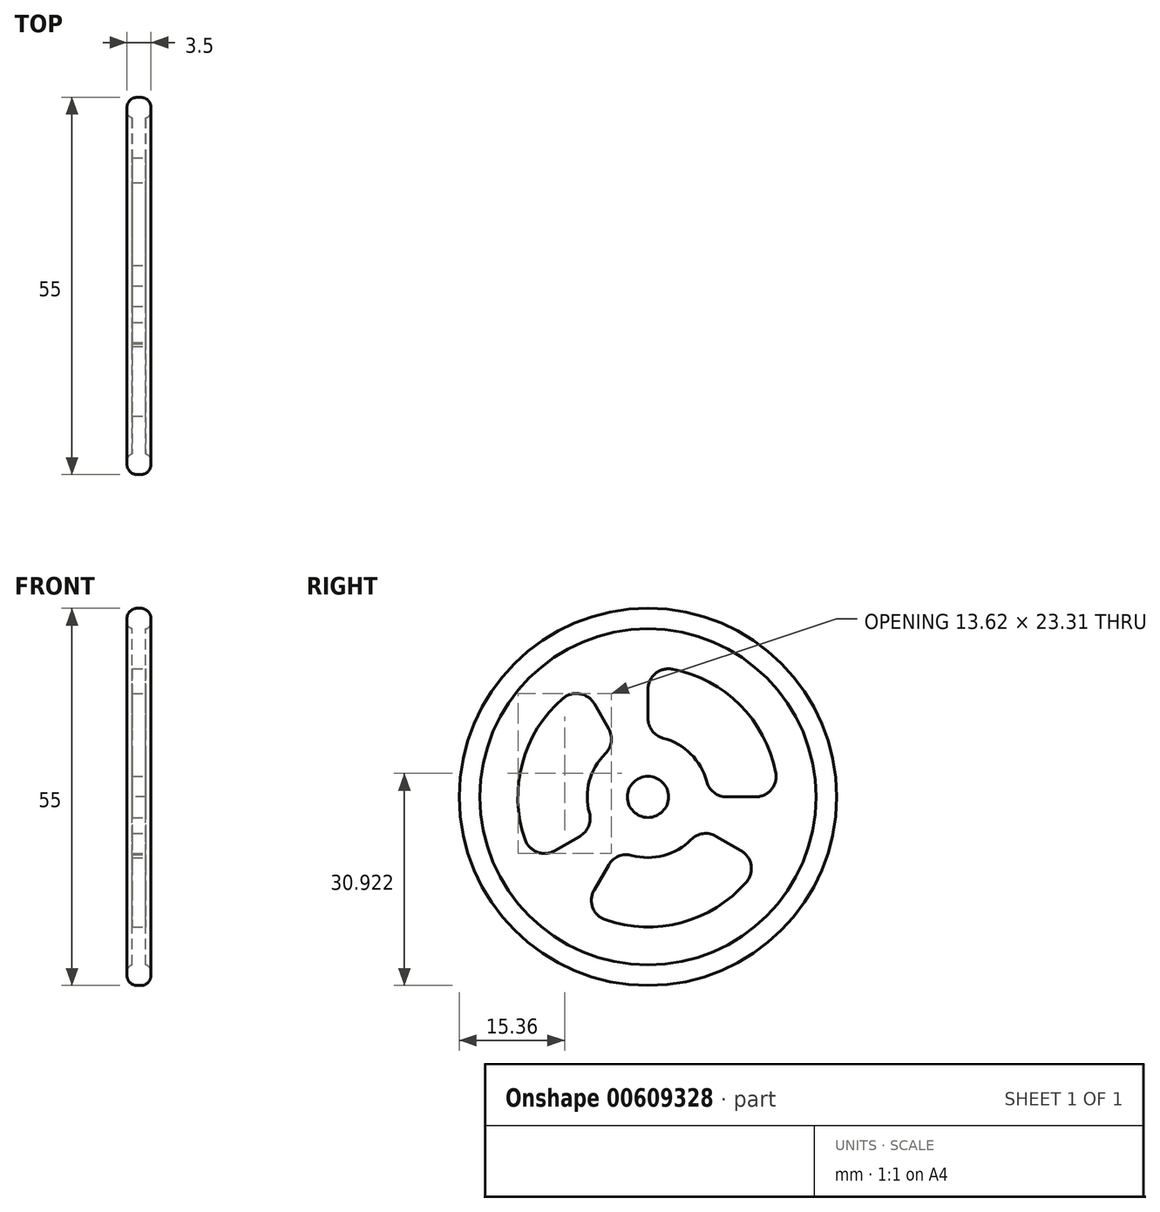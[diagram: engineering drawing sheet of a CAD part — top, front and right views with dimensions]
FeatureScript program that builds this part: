
annotation { "Feature Type Name" : "Feature", "Feature Type Description" : "" }
export const myFeature = defineFeature(function(context is Context, id is Id, definition is map)
    precondition{}
    {
        {
            var Q0;
            Q0=qCreatedBy(makeId("Right.planeOp"),FACE);
            var sketch = newSketch(context, id + "F0", { "sketchPlane" : qUnion([Q0])});
            skCircle(sketch, "E0", {"center": v(0, 0) * mm, "radius": 27.5 * mm});
            skCircle(sketch, "E1", {"center": v(0, 0) * mm, "radius": 24.5 * mm});
            skCircle(sketch, "E2", {"center": v(0, 0) * mm, "radius": 18.96 * mm});
            skCircle(sketch, "E3", {"center": v(0, 0) * mm, "radius": 8.85 * mm});
            skLineSegment(sketch, "E4", {"start": v(0, 18.96) * mm, "end": v(0, 8.85) * mm});
            skLineSegment(sketch, "E5", {"start": v(-7.66, -4.42) * mm, "end": v(-16.42, -9.48) * mm});
            skLineSegment(sketch, "E6", {"start": v(7.66, -4.42) * mm, "end": v(16.42, -9.48) * mm});
            skLineSegment(sketch, "E7", {"start": v(-4.42, 7.66) * mm, "end": v(-9.48, 16.42) * mm});
            skLineSegment(sketch, "E8.1.0", {"start": v(-4.42, -7.66) * mm, "end": v(-9.48, -16.42) * mm});
            skLineSegment(sketch, "E8.2.0", {"start": v(8.85, 0) * mm, "end": v(18.96, 0) * mm});
            skCircle(sketch, "E9", {"center": v(0, 0) * mm, "radius": 3 * mm});
            skSolve(sketch);
        }
        {
            var Q0;
            Q0=makeQuery(id+"F0.imprint","IMPRINT",FACE,{"disambiguationData":[TD([[makeQuery(id+"F0.imprint","IMPRINT",EDGE,{"derivedFrom":sQuery(id+"F0.wireOp",EDGE,"E1")}),1.0]])]});
            var Q1;
            {var subQ0=sQuery(id+"F0.wireOp",EDGE,"E3");var subQ1=makeQuery(id+"F0.imprint","INTERSECT",VERTEX,{"derivedFrom":[subQ0,sQuery(id+"F0.wireOp",EDGE,"E4")]});Q1=makeQuery(id+"F0.imprint","IMPRINT",FACE,{"disambiguationData":[TD([[makeQuery(id+"F0.imprint","IMPRINT",EDGE,{"disambiguationData":[TD([[subQ1,-1.0]])],"derivedFrom":subQ0}),1.0]])]});}
            var Q2;
            {var subQ0=sQuery(id+"F0.wireOp",EDGE,"E4");Q2=makeQuery(id+"F0.imprint","IMPRINT",FACE,{"disambiguationData":[TD([[makeQuery(id+"F0.imprint","IMPRINT",EDGE,{"derivedFrom":subQ0}),-1.0]])]});}
            var Q3;
            {var subQ0=sQuery(id+"F0.wireOp",EDGE,"E5");Q3=makeQuery(id+"F0.imprint","IMPRINT",FACE,{"disambiguationData":[TD([[makeQuery(id+"F0.imprint","IMPRINT",EDGE,{"derivedFrom":subQ0}),1.0]])]});}
            var Q4;
            {var subQ0=sQuery(id+"F0.wireOp",EDGE,"E6");Q4=makeQuery(id+"F0.imprint","IMPRINT",FACE,{"disambiguationData":[TD([[makeQuery(id+"F0.imprint","IMPRINT",EDGE,{"derivedFrom":subQ0}),1.0]])]});}
            extrude(context, id + "F1", {"entities" : qUnion([Q0, Q1, Q2, Q3, Q4]), "endBound" : BoundingType.SYMMETRIC, "oppositeDirection" : true, "depth" : 2 * mm, "offsetDistance" : 25.4 * mm});
        }
        {
            var Q0;
            Q0 = qSketchRegion(id + "F0", true);
            extrude(context, id + "F2", {"entities" : qUnion([Q0]), "operationType" : NewBodyOperationType.ADD, "endBound" : BoundingType.SYMMETRIC, "depth" : 3.5 * mm, "offsetDistance" : 25.4 * mm});
        }
        {
            var Q0;
            Q0=makeQuery(id+"F2.opExtrude","CAP_EDGE",EDGE,{"disambiguationData":[OSD([sQuery(id+"F0.wireOp",EDGE,"E0")])],"isStart":true});
            var Q1;
            Q1=makeQuery(id+"F2.opExtrude","CAP_EDGE",EDGE,{"disambiguationData":[OSD([sQuery(id+"F0.wireOp",EDGE,"E0")])],"isStart":false});
            fillet(context, id + "F3", {"entities" : qUnion([Q0, Q1]), "radius" : 1.5 * mm, "tangentPropagation" : true, "allowEdgeOverflow" : false});
        }
        {
            var Q0;
            Q0=makeQuery(id+"F2.opExtrude","CAP_EDGE",EDGE,{"disambiguationData":[OSD([sQuery(id+"F0.wireOp",EDGE,"E1")])],"isStart":false});
            var Q1;
            Q1=makeQuery(id+"F2.opExtrude","CAP_EDGE",EDGE,{"disambiguationData":[OSD([sQuery(id+"F0.wireOp",EDGE,"E1")])],"isStart":true});
            fillet(context, id + "F4", {"entities" : qUnion([Q0, Q1]), "radius" : 1 * mm, "tangentPropagation" : true, "allowEdgeOverflow" : false});
        }
        {
            var Q0;
            Q0=makeQuery(id+"F1.opExtrude","SWEPT_EDGE",EDGE,{"disambiguationData":[OSD([sQuery(id+"F0.wireOp",EDGE,"E2"),sQuery(id+"F0.wireOp",EDGE,"E5")])]});
            var Q1;
            Q1=makeQuery(id+"F1.opExtrude","SWEPT_EDGE",EDGE,{"disambiguationData":[OSD([sQuery(id+"F0.wireOp",EDGE,"E3"),sQuery(id+"F0.wireOp",EDGE,"E5")])]});
            var Q2;
            Q2=makeQuery(id+"F1.opExtrude","SWEPT_EDGE",EDGE,{"disambiguationData":[OSD([sQuery(id+"F0.wireOp",EDGE,"E3"),sQuery(id+"F0.wireOp",EDGE,"E7")])]});
            var Q3;
            Q3=makeQuery(id+"F1.opExtrude","SWEPT_EDGE",EDGE,{"disambiguationData":[OSD([sQuery(id+"F0.wireOp",EDGE,"E2"),sQuery(id+"F0.wireOp",EDGE,"E4")])]});
            var Q4;
            Q4=makeQuery(id+"F1.opExtrude","SWEPT_EDGE",EDGE,{"disambiguationData":[OSD([sQuery(id+"F0.wireOp",EDGE,"E2"),sQuery(id+"F0.wireOp",EDGE,"E7")])]});
            var Q5;
            Q5=makeQuery(id+"F1.opExtrude","SWEPT_EDGE",EDGE,{"disambiguationData":[OSD([sQuery(id+"F0.wireOp",EDGE,"E3"),sQuery(id+"F0.wireOp",EDGE,"E8.1.0")])]});
            var Q6;
            Q6=makeQuery(id+"F1.opExtrude","SWEPT_EDGE",EDGE,{"disambiguationData":[OSD([sQuery(id+"F0.wireOp",EDGE,"E3"),sQuery(id+"F0.wireOp",EDGE,"E6")])]});
            var Q7;
            Q7=makeQuery(id+"F1.opExtrude","SWEPT_EDGE",EDGE,{"disambiguationData":[OSD([sQuery(id+"F0.wireOp",EDGE,"E3"),sQuery(id+"F0.wireOp",EDGE,"E4")])]});
            var Q8;
            Q8=makeQuery(id+"F1.opExtrude","SWEPT_EDGE",EDGE,{"disambiguationData":[OSD([sQuery(id+"F0.wireOp",EDGE,"E3"),sQuery(id+"F0.wireOp",EDGE,"E8.2.0")])]});
            var Q9;
            Q9=makeQuery(id+"F1.opExtrude","SWEPT_EDGE",EDGE,{"disambiguationData":[OSD([sQuery(id+"F0.wireOp",EDGE,"E2"),sQuery(id+"F0.wireOp",EDGE,"E8.1.0")])]});
            var Q10;
            Q10=makeQuery(id+"F1.opExtrude","SWEPT_EDGE",EDGE,{"disambiguationData":[OSD([sQuery(id+"F0.wireOp",EDGE,"E2"),sQuery(id+"F0.wireOp",EDGE,"E6")])]});
            var Q11;
            Q11=makeQuery(id+"F1.opExtrude","SWEPT_EDGE",EDGE,{"disambiguationData":[OSD([sQuery(id+"F0.wireOp",EDGE,"E2"),sQuery(id+"F0.wireOp",EDGE,"E8.2.0")])]});
            fillet(context, id + "F5", {"entities" : qUnion([Q0, Q1, Q2, Q3, Q4, Q5, Q6, Q7, Q8, Q9, Q10, Q11]), "radius" : 3 * mm, "tangentPropagation" : true, "allowEdgeOverflow" : false});
        }
    });
